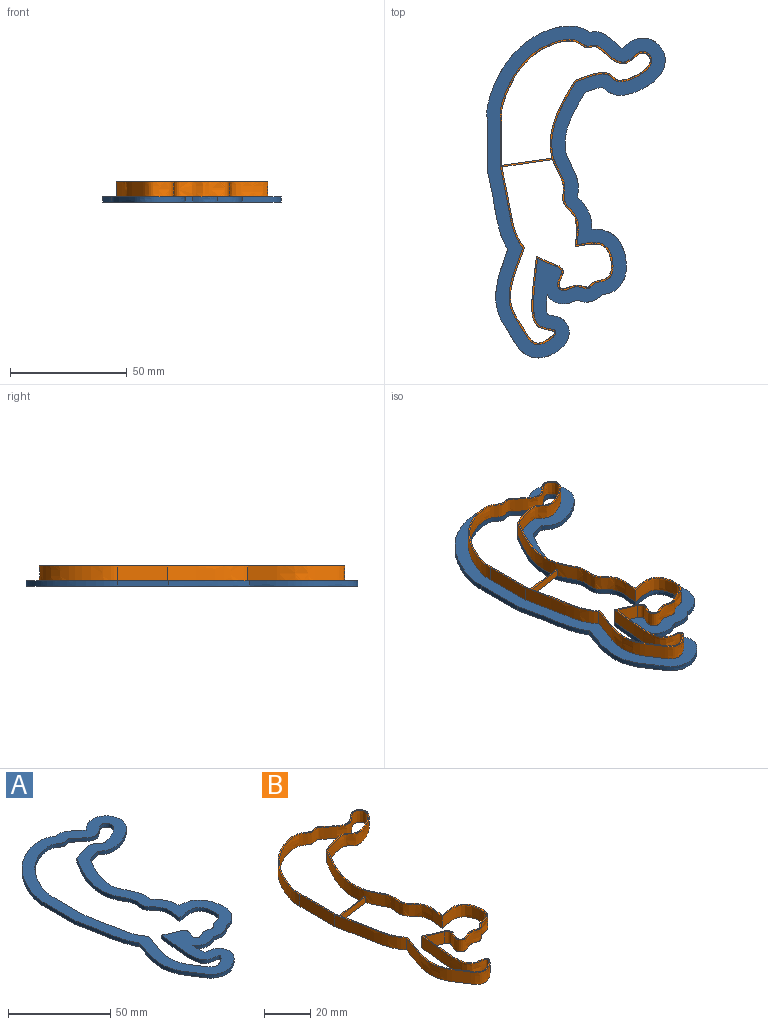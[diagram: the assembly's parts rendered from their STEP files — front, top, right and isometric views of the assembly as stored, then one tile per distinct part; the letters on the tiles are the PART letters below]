
ASSEMBLY  parts=2 mates=1
PART A: 22 faces, bbox 76.4x142.1x2.2 mm
  f0: plane 142.11x76.39mm, normal (0,0,1), area 2768mm2, adj f2,f3,f4,f5,f6,f7,f8,f9
  f1: plane 142.11x76.39mm, normal (0,0,-1), area 2768mm2, adj f2,f3,f4,f5,f6,f7,f8,f9
  f2: extruded ~8.44x2.21mm, area 18.7mm2, adj f0,f1,f3,f13
  f3: extruded ~12.75x3.86mm, area 31.7mm2, adj f0,f1,f2,f6
  f4: extruded ~44.85x8.61mm, area 105.6mm2, adj f0,f1,f10,f14
  f5: extruded ~28.31x14.73mm, area 94.7mm2, adj f0,f1,f6,f14
  f6: extruded ~10.47x2.94mm, area 25.3mm2, adj f0,f1,f3,f5
  f7: extruded ~43.92x39.32mm, area 147.9mm2, adj f0,f1,f8,f11
  f8: extruded ~14.08x7.09mm, area 36.2mm2, adj f0,f1,f7,f9
  f9: extruded ~26.78x24.39mm, area 132.1mm2, adj f0,f1,f8,f10
  f10: extruded ~7.43x2.21mm, area 17.1mm2, adj f0,f1,f4,f9
  f11: plane 21.79x2.21mm, normal (-1,0,0), area 48.2mm2, adj f0,f1,f7,f12
  f12: extruded ~34.53x8.86mm, area 79.3mm2, adj f0,f1,f11,f13
  f13: extruded ~46.38x31.41mm, area 187.6mm2, adj f0,f1,f2,f12
  f14: extruded ~13.67x6.15mm, area 34.2mm2, adj f0,f1,f4,f5
  f15: extruded ~63.55x32.51mm, area 277mm2, adj f0,f1,f16,f21
  f16: plane 21.38x2.21mm, normal (1,0,0), area 47.2mm2, adj f0,f1,f15,f17
  f17: extruded ~34.38x9.71mm, area 79.8mm2, adj f0,f1,f16,f18
  f18: extruded ~41x18.74mm, area 206.5mm2, adj f0,f1,f17,f19
  f19: extruded ~9.68x4.18mm, area 23.3mm2, adj f0,f1,f18,f20
  f20: extruded ~22.48x19.32mm, area 131.7mm2, adj f0,f1,f19,f21
  f21: extruded ~71.2x11.49mm, area 169.3mm2, adj f0,f1,f15,f20
PART B: 19 faces, bbox 65x131.3x6.4 mm
  f0: plane 131.28x64.96mm, normal (0,0,1), area 273.3mm2, adj f2,f3,f4,f5,f6,f7,f8,f9
  f1: plane 131.28x64.96mm, normal (0,0,-1), area 288.1mm2, adj f2,f3,f4,f5,f6,f7,f8,f9
  f2: extruded ~64.81x33.19mm, area 815.3mm2, adj f0,f1,f3,f8
  f3: plane 21.41x6.35mm, normal (-1,0,0), area 136mm2, adj f0,f1,f2,f4
  f4: extruded ~34.43x9.61mm, area 229.3mm2, adj f0,f1,f3,f5
  f5: extruded ~41.49x19.95mm, area 599.3mm2, adj f0,f1,f4,f6
  f6: extruded ~8.85x6.35mm, area 61mm2, adj f0,f1,f5,f7
  f7: extruded ~23.67x20.61mm, area 390.4mm2, adj f0,f1,f6,f8
  f8: extruded ~69.89x11.48mm, area 477.1mm2, adj f0,f1,f2,f7
  f9: extruded ~63.55x32.51mm, area 795.9mm2, adj f0,f1,f10,f15
  f10: plane 21.38x6.35mm, normal (1,0,0), area 133.6mm2, adj f0,f1,f9,f11,f16,f17
  f11: extruded ~34.38x9.71mm, area 229.4mm2, adj f0,f1,f10,f12,f18
  f12: extruded ~41x18.74mm, area 593.4mm2, adj f0,f1,f11,f13
  f13: extruded ~9.68x6.35mm, area 67mm2, adj f0,f1,f12,f14
  f14: extruded ~22.48x19.32mm, area 378.3mm2, adj f0,f1,f13,f15
  f15: extruded ~71.2x11.49mm, area 484.3mm2, adj f0,f1,f9,f14,f16,f17,f18
  f16: plane 21.63x3.72mm, normal (0,0,1), area 13.8mm2, adj f10,f15,f17,f18
  f17: plane 21.44x3.3mm, normal (-0.14,0.99,0), area 71.5mm2, adj f1,f10,f15,f16
  f18: plane 21.63x3.3mm, normal (0.14,-0.99,0), area 72.1mm2, adj f1,f11,f15,f16
PLACE A t=(-28.64,-16.66,-4.34)mm
PLACE B t=(-28.64,-16.66,-2.13)mm
MATE fastened A.f0 <-> B.f1  axis (0,0,1) through (-32.47,-54.84,-2.13)mm
